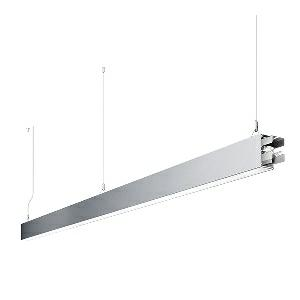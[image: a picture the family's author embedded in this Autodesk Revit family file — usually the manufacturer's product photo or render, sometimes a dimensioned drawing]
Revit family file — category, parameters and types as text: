
# Revit family: dotoo_line_-_dlp_3000_830_d_sta_00805852_7a24
name_source: partatom
category: Lighting Fixtures
units: mm (PartAtom-declared; Revit-internal decimal feet)

## family parameters
Cut with Voids When Loaded = No
Host = Face
Light Source = No
Part Type = Normal
Room Calculation Point = No
Round Connector Dimension = Use Diameter
Shared = No

## types (1)
- DOTOO.line - DLP 3000/830/D STA (1 x LED, 2650 lm, 3000K)
    Apparent Load = 26 VA
    Approval mark = CE
    CIE Flux Codes = 67 91 98 100 100
    Color Rendering = 80-89
    Color Temperature = 3000K
    Control Gear = Electronic ballast
    Default Elevation = 1800 mm
    Description = DLP 3000/830/D|Suspended luminaire|light source: LED|connected load: 220-240 V, 50/60 Hz|Power consumption: approx. 26 W|standby: approx. 0,15|luminous flux: 2650 lm|luminous efficacy: 101 lm/W|light distribution: Direct|direct ratio: approx. 100 %|colour temperature: Warm white, ca. 3000 K|color rendering index (CRI): >= 80|chromaticity tolerance:  3 SDCM|System of protection: IP 40|technology: Continuously dimmable|luminaire body|material: Sectional aluminium|colour: Silver|lamp cover: Acrylic (PMMA), Clear|mains lead: 2.00 m With free stranded wires|Fastening: Steel cable 0.3 - 0.7 m|glare control: Prism aperture|luminance(L65): <= 3000 cd/m|unified glare rating(4H 8H): <=  19|special features: DALI Load 1x, TouchDIM - dimming via standard switch, Through-wired, up to 18 m on one mains connection, Flicker-free, Suitable as emergency lighting, Start luminaire with mains connection, Mechanical and electrical connection of the individual modules without tools|
    Frequency = 50 Hz
    Height = 110 mm
    Lamp = 1 x LED
    Lamp Light Flux = 2650 lm
    Lamp count = 1
    Length = 2250 mm
    Luminous efficacy = 102 lm/W
    Manufacturer = Waldmann
    ModVariant = No
    Model = 00805852
    Mounting Place = Ceiling
    Mounting Type = Pendant
    Number of Poles = 1
    OnlyDefault = Yes
    Power Factor = 1
    Product Name = DOTOO.line - DLP 3000/830/D STA
    Product group = Suspended luminaire
    ProductGroupID = 9
    Protection Class = Protection class I
    Protection Degree = IP 40
    RLX_Detail_Level = 1
    RLX_Emergency_Light_Flux = 0 lm
    RLX_Emergency_Type = 0
    RLX_Emergency_Type_DB = No
    RlxData = <blob elided: 25069 chars, md5=5fb18fd9>
    Socket = socket
    Standby Power = 0 W
    System Light Flux = 2650 lm
    System Power = 26 W
    Type Comments = Product without accessories
    Type Image = 113316000-00692612.jpg
    URL = http://relux.com
    VarID = ---
    Voltage = 230 V
    Voltage Range = 220-240 V
    Weight = 0.00 kg
    Width = 60 mm  [stored 0.19685 ft]

note: [stored X ft] marks values corroborated as IEEE doubles in the binary element streams (Revit-internal decimal feet)

## geometry (parser evidence)
native form markers: Blend x4, Sweep x12
no freeform markers — native parametric forms only
